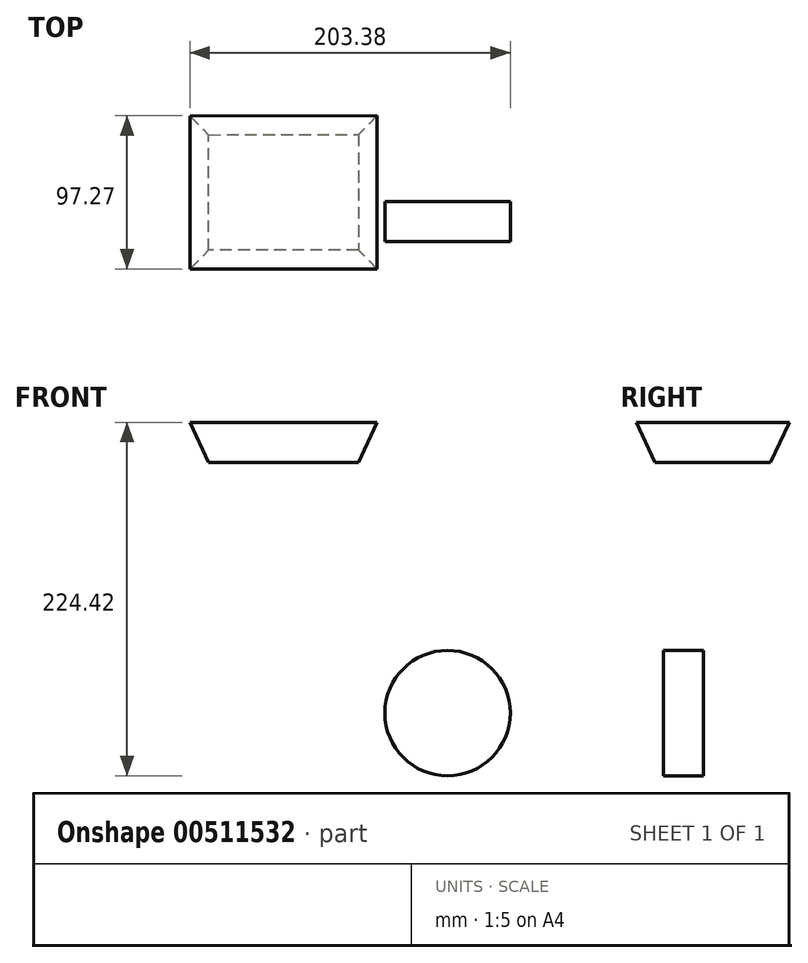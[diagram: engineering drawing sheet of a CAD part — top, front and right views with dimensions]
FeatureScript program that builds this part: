
annotation { "Feature Type Name" : "Feature", "Feature Type Description" : "" }
export const myFeature = defineFeature(function(context is Context, id is Id, definition is map)
    precondition{}
    {
        {
            var Q0;
            Q0=qCreatedBy(makeId("Top.planeOp"),FACE);
            var sketch = newSketch(context, id + "F0", { "sketchPlane" : qUnion([Q0])});
            skLineSegment(sketch, "E0", {"start": v(-46.01, 42.34) * mm, "end": v(-46.01, -30.98) * mm});
            skLineSegment(sketch, "E1", {"start": v(-46.01, -30.98) * mm, "end": v(49.1, -30.98) * mm});
            skLineSegment(sketch, "E2", {"start": v(49.1, -30.98) * mm, "end": v(49.1, 42.57) * mm});
            skLineSegment(sketch, "E3", {"start": v(49.1, 42.57) * mm, "end": v(-46.01, 42.34) * mm});
            skLineSegment(sketch, "E4", {"start": v(-46.01, 42.34) * mm, "end": v(-76.22, 95.62) * mm, "construction": true});
            skSolve(sketch);
        }
        {
            var Q0;
            Q0 = qSketchRegion(id + "F0", true);
            extrude(context, id + "F1", {"entities" : qUnion([Q0]), "depth" : 25.4 * mm, "hasDraft" : true, "draftAngle" : 25 * degree});
        }
        {
            var Q0;
            Q0=qCreatedBy(makeId("Front.planeOp"),FACE);
            var sketch = newSketch(context, id + "F2", { "sketchPlane" : qUnion([Q0])});
            skCircle(sketch, "E5", {"center": v(105.7, -159.21) * mm, "radius": 39.8 * mm});
            skSolve(sketch);
        }
        {
            var Q0;
            Q0 = qSketchRegion(id + "F2", true);
            extrude(context, id + "F3", {"entities" : qUnion([Q0]), "depth" : 25.4 * mm});
        }
    });
